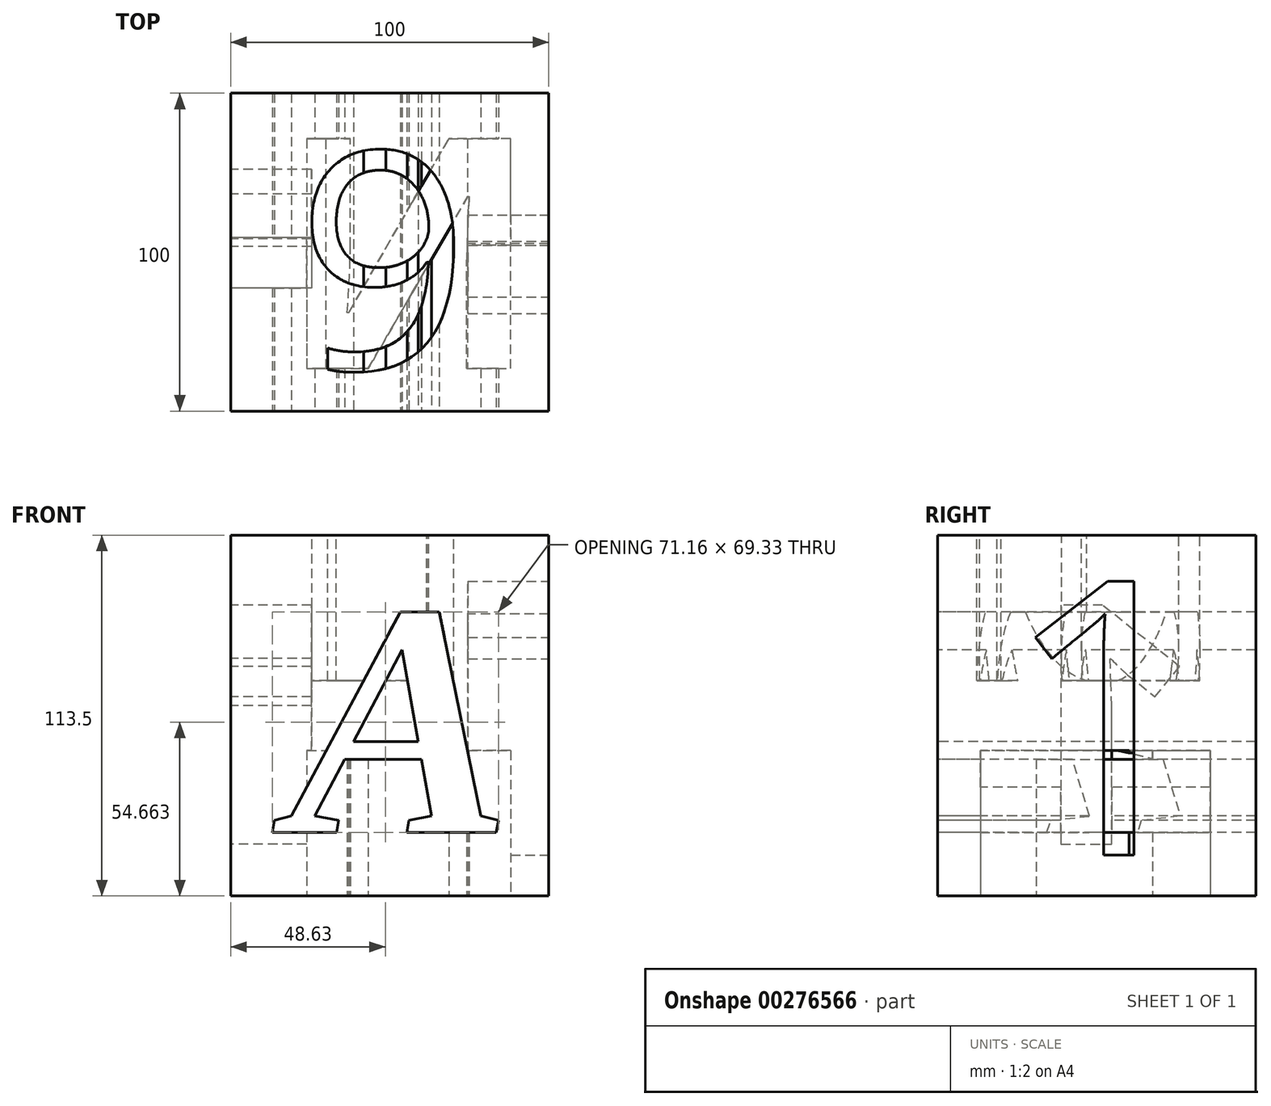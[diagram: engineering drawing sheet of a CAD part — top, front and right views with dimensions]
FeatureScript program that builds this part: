
annotation { "Feature Type Name" : "Feature", "Feature Type Description" : "" }
export const myFeature = defineFeature(function(context is Context, id is Id, definition is map)
    precondition{}
    {
        {
            var Q0;
            Q0=qCreatedBy(makeId("Front.planeOp"),FACE);
            var sketch = newSketch(context, id + "F0", { "sketchPlane" : qUnion([Q0])});
            skLineSegment(sketch, "E0.bottom", {"start": v(50, -56.75) * mm, "end": v(-50, -56.75) * mm});
            skLineSegment(sketch, "E0.top", {"start": v(50, 56.75) * mm, "end": v(-50, 56.75) * mm});
            skLineSegment(sketch, "E0.left", {"start": v(50, -56.75) * mm, "end": v(50, 56.75) * mm});
            skLineSegment(sketch, "E0.right", {"start": v(-50, -56.75) * mm, "end": v(-50, 56.75) * mm});
            skPoint(sketch, "E0.middle", {"position": v(0, 0) * mm});
            skSolve(sketch);
        }
        {
            var Q0;
            Q0=makeQuery(id+"F0.imprint","IMPRINT",FACE,{"disambiguationData":[TD([[makeQuery(id+"F0.imprint","IMPRINT",EDGE,{"derivedFrom":sQuery(id+"F0.wireOp",EDGE,"E0.bottom")}),-1.0]])]});
            extrude(context, id + "F1", {"entities" : qUnion([Q0]), "depth" : 100 * mm});
        }
        {
            var Q0;
            Q0=makeQuery(id+"F1.opExtrude","CAP_FACE",FACE,{"disambiguationData":[OSD([sQuery(id+"F0.wireOp",EDGE,"E0.bottom"),sQuery(id+"F0.wireOp",EDGE,"E0.top"),sQuery(id+"F0.wireOp",EDGE,"E0.left"),sQuery(id+"F0.wireOp",EDGE,"E0.right")])],"isStart":false});
            var sketch = newSketch(context, id + "F2", { "sketchPlane" : qUnion([Q0])});
            skText(sketch, "E1", { "text": "A", "fontName": "Tinos-BoldItalic.ttf"});
            const initialGuessF2  = {"E1": [-0.03152, -0.03675, 1, 0, 0.07561]};
            skSetInitialGuess(sketch, initialGuessF2);
            skSolve(sketch);
        }
        {
            var Q0;
            Q0=makeQuery(id+"F1.opExtrude","SWEPT_FACE",FACE,{"disambiguationData":[OSD([sQuery(id+"F0.wireOp",EDGE,"E0.left")])]});
            var sketch = newSketch(context, id + "F3", { "sketchPlane" : qUnion([Q0])});
            skSolve(sketch);
        }
        {
            var Q0;
            Q0=makeQuery(id+"F1.opExtrude","SWEPT_FACE",FACE,{"disambiguationData":[OSD([sQuery(id+"F0.wireOp",EDGE,"E0.right")])]});
            var sketch = newSketch(context, id + "F4", { "sketchPlane" : qUnion([Q0])});
            skText(sketch, "E2", { "text": "1", "fontName": "OpenSans-Bold.ttf"});
            const initialGuessF4  = {"E2": [0.0178, -0.0404, 1, 0, 0.07574]};
            skSetInitialGuess(sketch, initialGuessF4);
            skSolve(sketch);
        }
        {
            var Q0;
            Q0=makeQuery(id+"F1.opExtrude","SWEPT_FACE",FACE,{"disambiguationData":[OSD([sQuery(id+"F0.wireOp",EDGE,"E0.bottom")])]});
            var sketch = newSketch(context, id + "F5", { "sketchPlane" : qUnion([Q0])});
            skSolve(sketch);
        }
        {
            var Q0;
            {var subQ0=sQuery(id+"F0.wireOp",EDGE,"E0.left");Q0=makeQuery(id+"F3.imprint","IMPRINT",FACE,{"disambiguationData":[TD([[makeQuery(id+"F3.imprint","IMPRINT",EDGE,{"derivedFrom":makeQuery(id+"F1.opExtrude","CAP_EDGE",EDGE,{"disambiguationData":[OSD([subQ0])],"isStart":true})}),1.0]])]});}
            var sketch = newSketch(context, id + "F6", { "sketchPlane" : qUnion([Q0])});
            skText(sketch, "E3", { "text": "1", "fontName": "OpenSans-Regular.ttf"});
            const initialGuessF6  = {"E3": [-0.08043, -0.04387, 1, 0, 0.08682]};
            skSetInitialGuess(sketch, initialGuessF6);
            skSolve(sketch);
        }
        {
            var Q0;
            Q0=makeQuery(id+"F1.opExtrude","SWEPT_FACE",FACE,{"disambiguationData":[OSD([sQuery(id+"F0.wireOp",EDGE,"E0.top")])]});
            var sketch = newSketch(context, id + "F7", { "sketchPlane" : qUnion([Q0])});
            skText(sketch, "E4", { "text": "9", "fontName": "OpenSans-Regular.ttf"});
            const initialGuessF7  = {"E4": [-0.02942, -0.08685, 1, 0, 0.06886]};
            skSetInitialGuess(sketch, initialGuessF7);
            skSolve(sketch);
        }
        {
            var Q0;
            {var subQ0=sQuery(id+"F0.wireOp",EDGE,"E0.bottom");Q0=makeQuery(id+"F5.imprint","IMPRINT",FACE,{"disambiguationData":[TD([[makeQuery(id+"F5.imprint","IMPRINT",EDGE,{"derivedFrom":makeQuery(id+"F1.opExtrude","CAP_EDGE",EDGE,{"disambiguationData":[OSD([subQ0])],"isStart":true})}),-1.0]])]});}
            var sketch = newSketch(context, id + "F8", { "sketchPlane" : qUnion([Q0])});
            skText(sketch, "E5", { "text": "N", "fontName": "OpenSans-Bold.ttf"});
            const initialGuessF8  = {"E5": [-0.0352, 0.01435, 1, 0, 0.0729]};
            skSetInitialGuess(sketch, initialGuessF8);
            skSolve(sketch);
        }
        {
            var Q0;
            Q0=makeQuery(id+"F2.imprint","IMPRINT",FACE,{"disambiguationData":[TD([[makeQuery(id+"F2.imprint","IMPRINT",EDGE,{"derivedFrom":sQuery(id+"F2.wireOp",EDGE,"E1.sketch_text.stroke-0")}),-1.0]])]});
            extrude(context, id + "F9", {"entities" : qUnion([Q0]), "operationType" : NewBodyOperationType.REMOVE, "oppositeDirection" : true, "depth" : 100.08 * mm});
        }
        {
            var Q0;
            Q0 = qSketchRegion(id + "F6", true);
            extrude(context, id + "F10", {"entities" : qUnion([Q0]), "operationType" : NewBodyOperationType.REMOVE, "oppositeDirection" : true, "depth" : 25.4 * mm});
        }
        {
            var Q0;
            Q0=makeQuery(id+"F4.imprint","IMPRINT",FACE,{"disambiguationData":[TD([[makeQuery(id+"F4.imprint","IMPRINT",EDGE,{"derivedFrom":sQuery(id+"F4.wireOp",EDGE,"E2.sketch_text.stroke-0")}),-1.0]])]});
            extrude(context, id + "F11", {"entities" : qUnion([Q0]), "operationType" : NewBodyOperationType.REMOVE, "oppositeDirection" : true, "depth" : 25.4 * mm});
        }
        {
            var Q0;
            Q0 = qSketchRegion(id + "F7", true);
            extrude(context, id + "F12", {"entities" : qUnion([Q0]), "operationType" : NewBodyOperationType.REMOVE, "oppositeDirection" : true, "depth" : 45.72 * mm});
        }
        {
            var Q0;
            Q0 = qSketchRegion(id + "F8", true);
            extrude(context, id + "F13", {"entities" : qUnion([Q0]), "operationType" : NewBodyOperationType.REMOVE, "oppositeDirection" : true, "depth" : 45.72 * mm});
        }
    });
